MODEL slx_b836e96fd809
CONFIG AbsTol = auto
CONFIG FixedStep = 0.1
CONFIG MaxStep = auto
CONFIG MinStep = auto
CONFIG RelTol = 1e-3
CONFIG SampleTimeConstraint = Unconstrained
CONFIG Solver = ode3
CONFIG SolverMode = Auto
CONFIG SolverName = ode3
CONFIG StartTime = 0.0
CONFIG StopTime = 10.0
BLOCK [Memory] Memory
BLOCK [Mux] Mux
  DisplayOption = bar
  Inputs = 2
  Ports = [2, 1]
BLOCK [Mux] Mux1
  DisplayOption = bar
  Inputs = 2
  Ports = [2, 1]
BLOCK [Scope] Scope
  NumInputPorts = 2
  Ports = [2]
  ScopeSpecificationString = Simulink.scopes.TimeScopeBlockCfg('CurrentConfiguration', extmgr.ConfigurationSet(extmgr.Configuration('Core','General UI',true),extmgr.Configuration('Core','Source UI',true),extmgr.Configuration('Sources','WiredSimulink',true,'DataLoggingSaveFormat','StructureWithTime','DataLoggingLimitDataPoints',true,'DataLoggingDecimation','1','DataLoggingDecimateData',true),extmgr.Configuration('Visuals','Tim...<+2289ch>
BLOCK [SignalGenerator] Signal Generator
  Frequency = 0.5
  Ports = [0, 1]
BLOCK [UnitDelay] Unit Delay
  InputProcessing = Elements as channels (sample based)
  SampleTime = -1
LINE Memory:1 -> Mux1:2
LINE Mux1:1 -> Scope:2
LINE Mux:1 -> Scope:1
LINE Signal Generator:1 -> Memory:1
LINE Signal Generator:1 -> Mux1:1
LINE Signal Generator:1 -> Mux:1
LINE Signal Generator:1 -> Unit Delay:1
LINE Unit Delay:1 -> Mux:2
